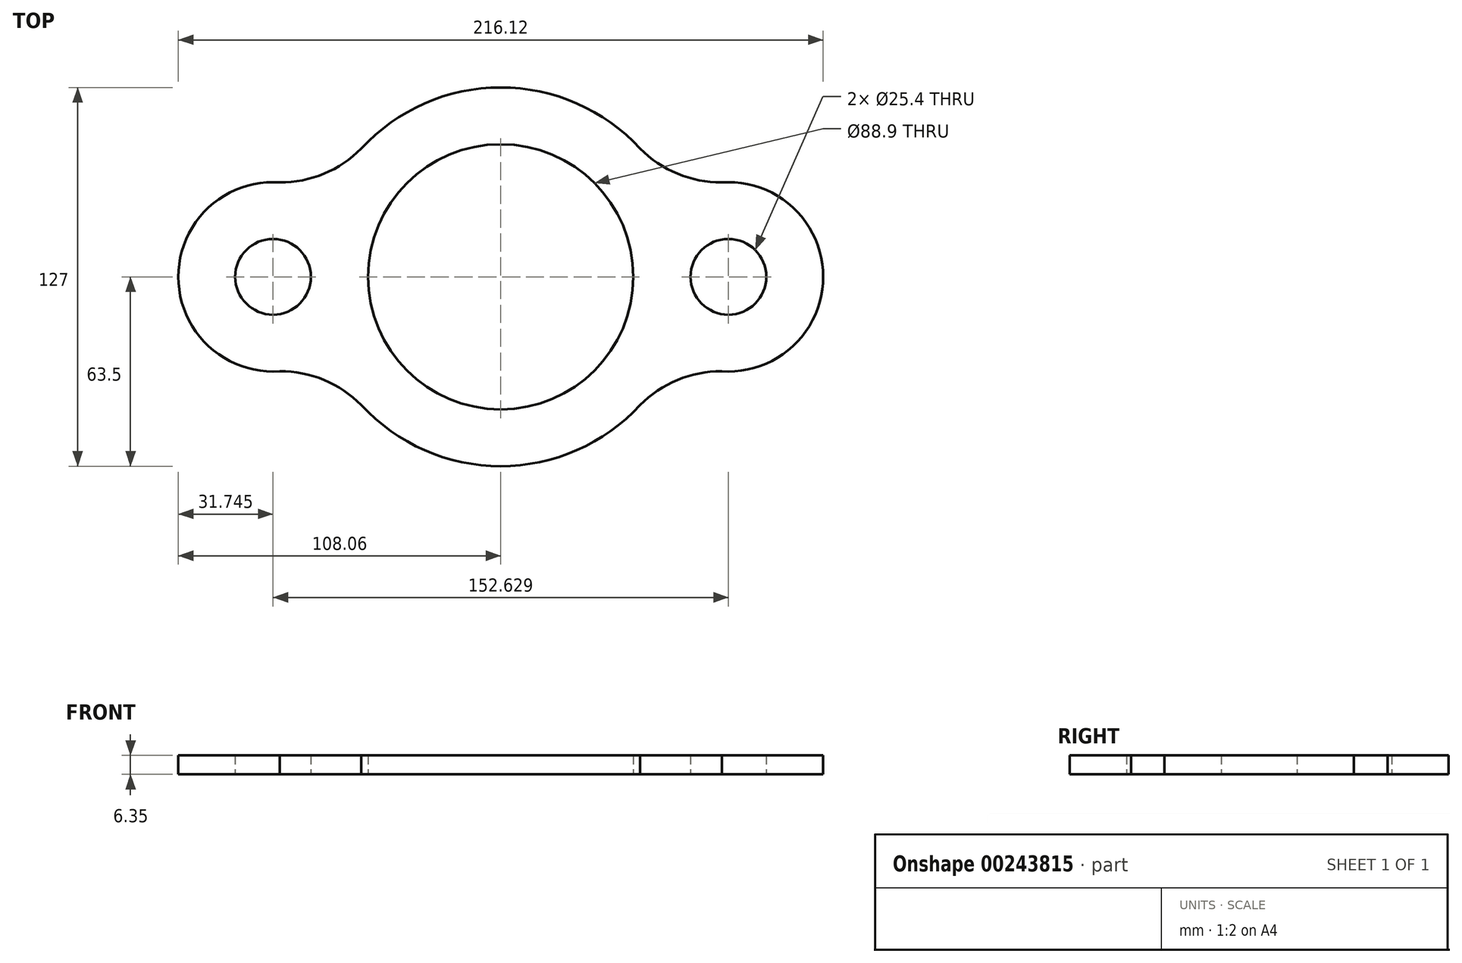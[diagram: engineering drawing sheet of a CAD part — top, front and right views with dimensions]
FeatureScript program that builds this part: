
annotation { "Feature Type Name" : "Feature", "Feature Type Description" : "" }
export const myFeature = defineFeature(function(context is Context, id is Id, definition is map)
    precondition{}
    {
        {
            var Q0;
            Q0=qCreatedBy(makeId("Top.planeOp"),FACE);
            var sketch = newSketch(context, id + "F0", { "sketchPlane" : qUnion([Q0])});
            skArc(sketch, "E0", {"start": v(-46.72, -43) * mm, "mid": v(0, -63.5) * mm, "end": v(46.72, -43) * mm});
            skCircle(sketch, "E1", {"center": v(0, 0) * mm, "radius": 44.45 * mm});
            skArc(sketch, "E2", {"start": v(-74.09, 31.67) * mm, "mid": v(-108.06, 0) * mm, "end": v(-74.09, -31.67) * mm});
            skCircle(sketch, "E3", {"center": v(-76.31, 0) * mm, "radius": 12.7 * mm});
            skArc(sketch, "E4", {"start": v(-45.58, -44.21) * mm, "mid": v(-59.5, -34.47) * mm, "end": v(-76.29, -31.75) * mm});
            skArc(sketch, "E5.MirrorCS", {"start": v(74.09, 31.67) * mm, "mid": v(108.06, 0) * mm, "end": v(74.09, -31.67) * mm});
            skCircle(sketch, "E6.MirrorC", {"center": v(76.31, 0) * mm, "radius": 12.7 * mm});
            skArc(sketch, "E7.trimOffspring", {"start": v(46.72, 43) * mm, "mid": v(0, 63.5) * mm, "end": v(-46.72, 43) * mm});
            skArc(sketch, "E8.MirrorCS", {"start": v(45.58, -44.21) * mm, "mid": v(59.5, -34.47) * mm, "end": v(76.29, -31.75) * mm});
            skArc(sketch, "E9.MirrorCS", {"start": v(45.58, 44.21) * mm, "mid": v(59.5, 34.47) * mm, "end": v(76.29, 31.75) * mm});
            skArc(sketch, "E10.MirrorCS", {"start": v(-45.58, 44.21) * mm, "mid": v(-59.5, 34.47) * mm, "end": v(-76.29, 31.75) * mm});
            skPoint(sketch, "E11.orphan", {"position": v(-57.97, 25.91) * mm});
            skPoint(sketch, "E12.orphan", {"position": v(-57.97, -25.91) * mm});
            skPoint(sketch, "E13.orphan", {"position": v(57.97, 25.91) * mm});
            skPoint(sketch, "E14.orphan", {"position": v(57.97, -25.91) * mm});
            skLineSegment(sketch, "E15", {"start": v(-76.7, -75.5) * mm, "end": v(75.7, -75.5) * mm});
            skSolve(sketch);
        }
        {
            var Q0;
            Q0=makeQuery(id+"F0.imprint","IMPRINT",FACE,{"disambiguationData":[TD([[makeQuery(id+"F0.imprint","IMPRINT",EDGE,{"derivedFrom":sQuery(id+"F0.wireOp",EDGE,"E0")}),1.0]])]});
            extrude(context, id + "F1", {"entities" : qUnion([Q0]), "depth" : 6.35 * mm});
        }
        {
            var Q0;
            Q0 = qSketchRegion(id + "F0", true);
            extrude(context, id + "F2", {"entities" : qUnion([Q0]), "operationType" : NewBodyOperationType.ADD, "depth" : 6.35 * mm});
        }
        {
            var Q0;
            Q0=makeQuery(id+"F1.opExtrude","SWEPT_BODY",BODY,{"disambiguationData":[OSD([sQuery(id+"F0.wireOp",EDGE,"E0"),sQuery(id+"F0.wireOp",EDGE,"E2")])]});
            var Q1;
            Q1=qCreatedBy(makeId("Right.planeOp"),FACE);
            mirror(context, id + "F3", {"operationType" : NewBodyOperationType.ADD, "entities" : qUnion([Q0]), "mirrorPlane" : qUnion([Q1])});
        }
        {
            var Q0;
            Q0=makeQuery(id+"F1.opExtrude","SWEPT_BODY",BODY,{"disambiguationData":[OSD([sQuery(id+"F0.wireOp",EDGE,"E0"),sQuery(id+"F0.wireOp",EDGE,"E1"),sQuery(id+"F0.wireOp",EDGE,"E2"),sQuery(id+"F0.wireOp",EDGE,"E4")])]});
            var Q1;
            Q1=qCreatedBy(makeId("Front.planeOp"),FACE);
            mirror(context, id + "F4", {"operationType" : NewBodyOperationType.ADD, "entities" : qUnion([Q0]), "mirrorPlane" : qUnion([Q1])});
        }
    });
